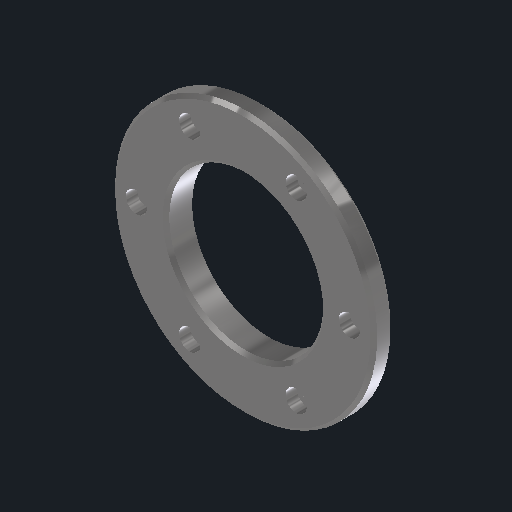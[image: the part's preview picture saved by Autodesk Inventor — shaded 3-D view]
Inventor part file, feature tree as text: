
AUTODESK INVENTOR PART (.ipt)
format: ipt  version: 2022 (Build 260153000, 153)  size: 199,680 bytes
history: native  units: mm
features: sketch x3, chamfer x3, plane x2, extrude x2, reference x2, other x2, hole x1
ambient origin geometry x8: Origin, YZ Plane, XZ Plane, XY Plane, X Axis, Y Axis, Z Axis, Center Point
bodies: Body1 (feature_tree)
feature tree (15):
  sketch  "Sketch1"  dims[d0=47.0mm d26=10.0mm d27=0.0mm]
  plane  "Work Plane3"
  extrude  "Extrusion3"  Depth=10.0mm TaperAngle=0.0deg
  sketch  "Sketch4"  dims[d28=10.0mm d29=0.0mm d30=2.0mm d31=2.0mm d32=45.0deg d33=1.0mm d34=2.0mm d35=45.0deg]
  plane  "Work Plane4"
  extrude  "Extrusion4"  Depth=2.0mm TaperAngle=45.0deg
  chamfer  "Chamfer4"  Distance=1.0mm Angle=45.0deg
  chamfer  "Chamfer5"  Distance=60.0mm Angle=360.0deg
  hole  "Hole2"  [1 undecoded]
  chamfer  "Chamfer6"  [1 undecoded]
  reference  "Reference1"
  reference  "Reference3"
  sketch  "Sketch5"  dims[d36=65.0mm d37=60.0mm d39=360.0deg d41=3.4mm d42=6.0mm d43=6.5mm d44=3.4mm d45=90.0deg d46=8.0mm d47=20.594885mm d48=1.0mm d49=2.0mm d50=45.0deg]
  other  "SistemaElevacionV2.iam"
  other  "Soporte:1"
note: 2 required parameter values undecoded (feature->parameter linkage not recoverable at this tier; creation-order binding heuristic only, values carry confidence <= 0.55)
